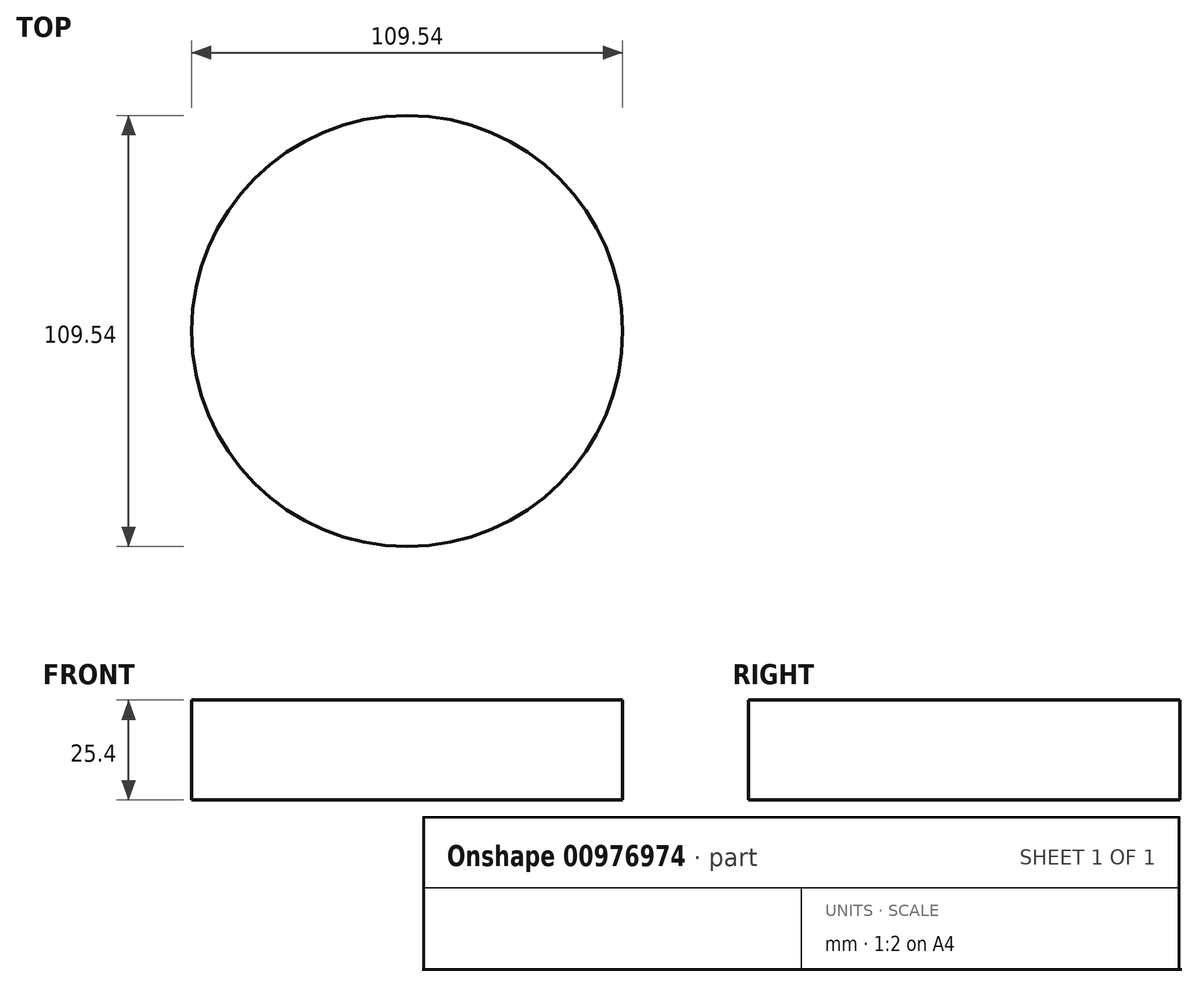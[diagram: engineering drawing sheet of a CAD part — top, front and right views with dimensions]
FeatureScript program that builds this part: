
annotation { "Feature Type Name" : "Feature", "Feature Type Description" : "" }
export const myFeature = defineFeature(function(context is Context, id is Id, definition is map)
    precondition{}
    {
        {
            var Q0;
            Q0=qCreatedBy(makeId("Top.planeOp"),FACE);
            var sketch = newSketch(context, id + "F0", { "sketchPlane" : qUnion([Q0])});
            skCircle(sketch, "E0", {"center": v(0, 0) * mm, "radius": 54.77 * mm});
            skSolve(sketch);
        }
        {
            var Q0;
            Q0=makeQuery(id+"F0.imprint","IMPRINT",FACE,{"disambiguationData":[TD([[makeQuery(id+"F0.imprint","IMPRINT",EDGE,{"derivedFrom":sQuery(id+"F0.wireOp",EDGE,"E0")}),1.0]])]});
            var Q1;
            Q1=sQuery(id+"F0.wireOp",EDGE,"E0");
            extrude(context, id + "F1", {"entities" : qUnion([Q0]), "surfaceEntities" : qUnion([Q1]), "depth" : 25.4 * mm, "offsetDistance" : 25.4 * mm});
        }
    });
